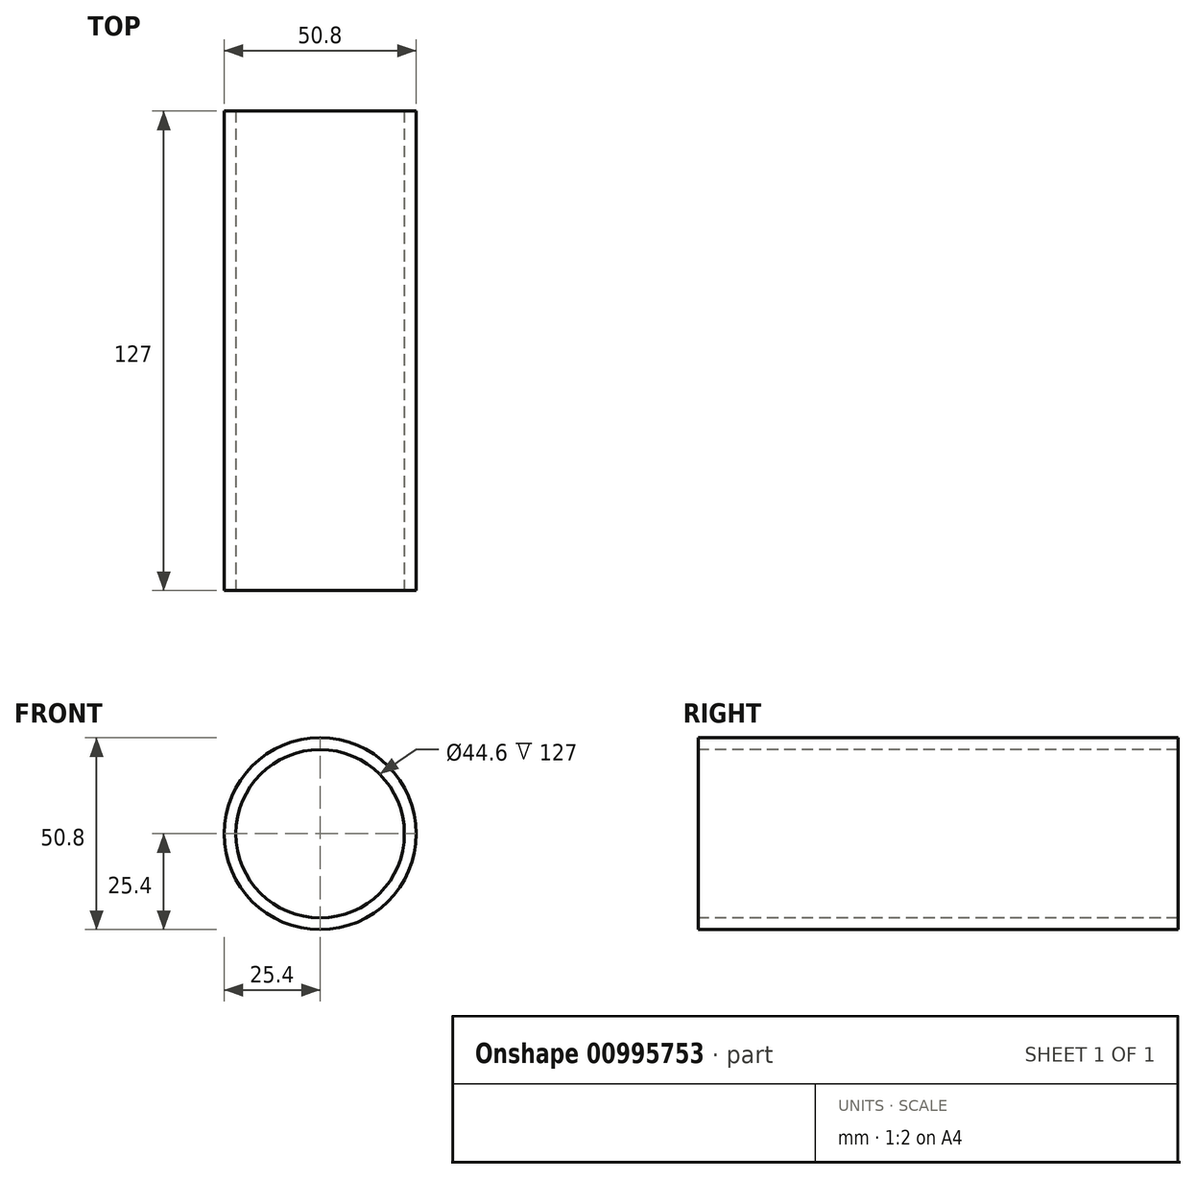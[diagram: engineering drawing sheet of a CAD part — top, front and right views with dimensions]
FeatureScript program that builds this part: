
annotation { "Feature Type Name" : "Feature", "Feature Type Description" : "" }
export const myFeature = defineFeature(function(context is Context, id is Id, definition is map)
    precondition{}
    {
        {
            var Q0;
            Q0=qCreatedBy(makeId("Front.planeOp"),FACE);
            var sketch = newSketch(context, id + "F0", { "sketchPlane" : qUnion([Q0])});
            skCircle(sketch, "E0", {"center": v(0, 0) * mm, "radius": 22.3 * mm});
            skCircle(sketch, "E1", {"center": v(0, 0) * mm, "radius": 25.4 * mm});
            skSolve(sketch);
        }
        {
            var Q0;
            Q0=makeQuery(id+"F0.imprint","IMPRINT",FACE,{"disambiguationData":[TD([[makeQuery(id+"F0.imprint","IMPRINT",EDGE,{"derivedFrom":sQuery(id+"F0.wireOp",EDGE,"E0")}),-1.0]])]});
            extrude(context, id + "F1", {"entities" : qUnion([Q0]), "oppositeDirection" : true, "depth" : 127 * mm, "offsetDistance" : 25 * mm});
        }
    });
